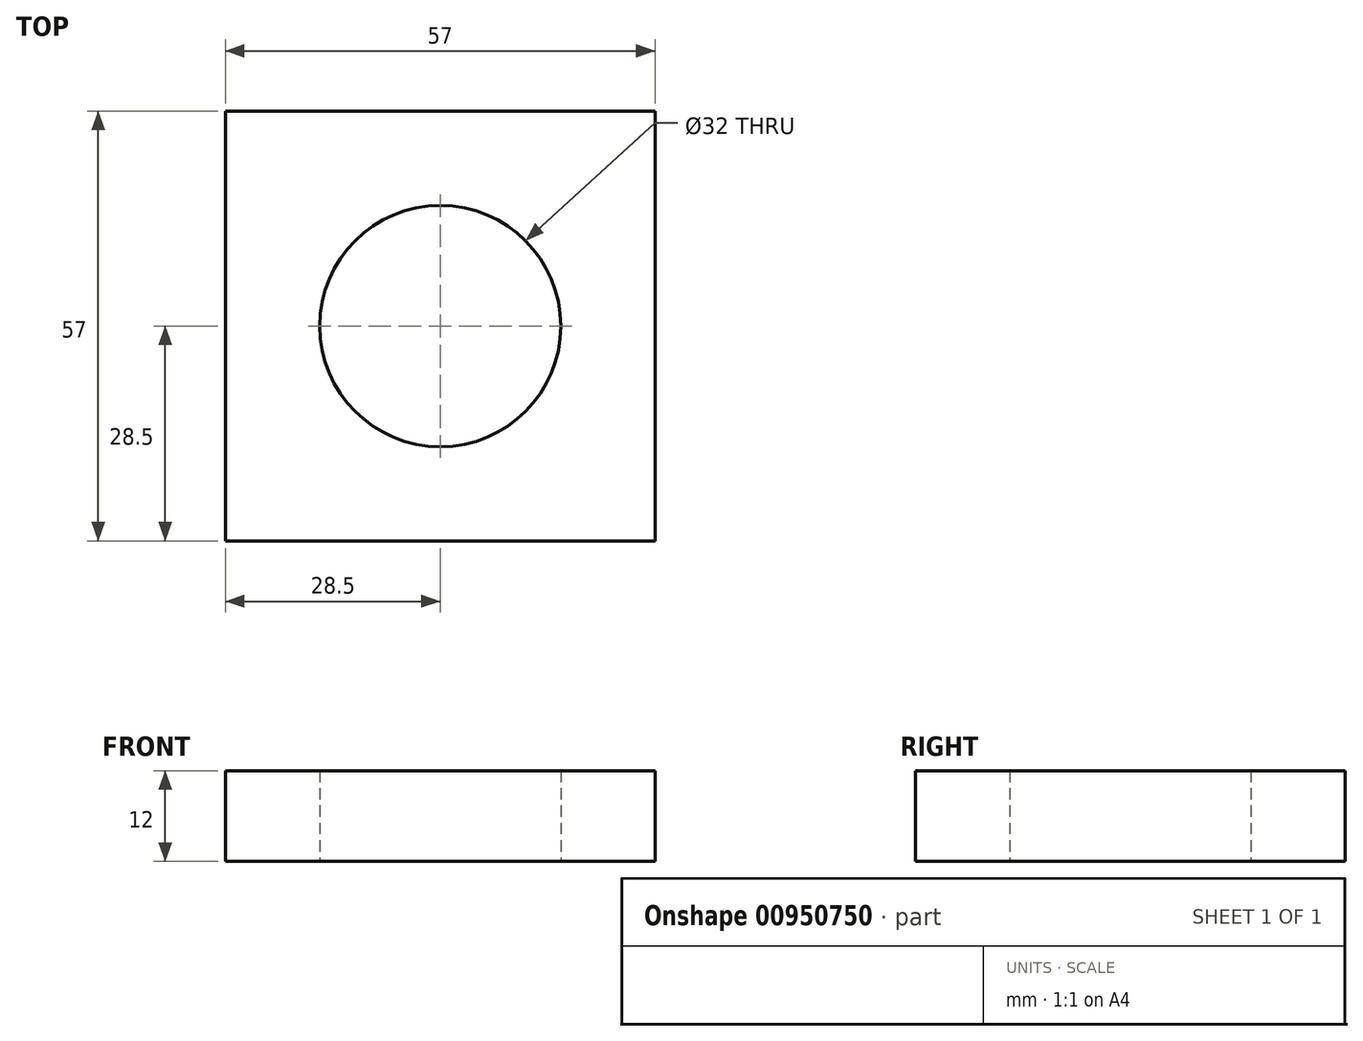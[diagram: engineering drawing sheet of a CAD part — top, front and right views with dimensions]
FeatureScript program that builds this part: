
annotation { "Feature Type Name" : "Feature", "Feature Type Description" : "" }
export const myFeature = defineFeature(function(context is Context, id is Id, definition is map)
    precondition{}
    {
        {
            var Q0;
            Q0=qCreatedBy(makeId("Top.planeOp"), FACE);
            var sketch = newSketch(context, id + "F0", { "sketchPlane" : qUnion([Q0])});
            skCircle(sketch, "E0", {"center": v(0, 0) * mm, "radius": 16 * mm});
            skFitSpline(sketch, "E1.0", {"points": [v(5.85, 0) * mm, v(5.85, 0.17) * mm, v(5.82, 0.5) * mm, v(5.75, 1) * mm, v(5.63, 1.48) * mm, v(5.47, 1.96) * mm, v(5.27, 2.42) * mm, v(5.04, 2.85) * mm, v(4.76, 3.27) * mm, v(4.46, 3.66) * mm, v(4.12, 4.02) * mm, v(3.75, 4.35) * mm, v(3.36, 4.65) * mm, v(2.94, 4.9) * mm, v(2.5, 5.13) * mm, v(2.05, 5.32) * mm, v(1.58, 5.46) * mm, v(1.1, 5.57) * mm, v(0.62, 5.63) * mm, v(0.14, 5.65) * mm, v(-0.35, 5.63) * mm, v(-0.83, 5.57) * mm, v(-1.3, 5.46) * mm, v(-1.76, 5.32) * mm, v(-2.2, 5.14) * mm, v(-2.63, 4.92) * mm, v(-3.04, 4.67) * mm, v(-3.42, 4.38) * mm, v(-3.78, 4.06) * mm, v(-4.1, 3.72) * mm, v(-4.4, 3.35) * mm, v(-4.66, 2.95) * mm, v(-4.88, 2.53) * mm, v(-5.07, 2.1) * mm, v(-5.22, 1.65) * mm, v(-5.34, 1.2) * mm, v(-5.4, 0.73) * mm, v(-5.44, 0.27) * mm, v(-5.43, -0.2) * mm, v(-5.38, -0.66) * mm, v(-5.3, -1.12) * mm, v(-5.17, -1.57) * mm, v(-5, -2) * mm, v(-4.8, -2.42) * mm, v(-4.57, -2.81) * mm, v(-4.3, -3.19) * mm, v(-4, -3.54) * mm, v(-3.68, -3.86) * mm, v(-3.32, -4.15) * mm, v(-2.95, -4.41) * mm, v(-2.55, -4.64) * mm, v(-2.14, -4.83) * mm, v(-1.72, -4.99) * mm, v(-1.28, -5.1) * mm, v(-0.83, -5.18) * mm, v(-0.39, -5.23) * mm, v(0.06, -5.23) * mm, v(0.51, -5.2) * mm, v(0.95, -5.12) * mm, v(1.39, -5) * mm, v(1.8, -4.86) * mm, v(2.21, -4.67) * mm, v(2.6, -4.46) * mm, v(2.96, -4.2) * mm, v(3.3, -3.93) * mm, v(3.62, -3.62) * mm, v(3.91, -3.3) * mm, v(4.17, -2.94) * mm, v(4.4, -2.56) * mm, v(4.6, -2.17) * mm, v(4.75, -1.77) * mm, v(4.87, -1.35) * mm, v(4.96, -0.92) * mm, v(5, -0.5) * mm, v(5.02, -0.06) * mm, v(5, 0.37) * mm, v(4.94, 0.8) * mm, v(4.84, 1.21) * mm, v(4.7, 1.62) * mm, v(4.54, 2.01) * mm, v(4.34, 2.39) * mm, v(4.1, 2.75) * mm, v(3.85, 3.08) * mm, v(3.56, 3.4) * mm, v(3.25, 3.68) * mm, v(2.92, 3.93) * mm, v(2.56, 4.16) * mm, v(2.2, 4.35) * mm, v(1.8, 4.51) * mm, v(1.4, 4.64) * mm, v(1, 4.73) * mm, v(0.6, 4.8) * mm, v(0.18, 4.81) * mm, v(-0.24, 4.8) * mm, v(-0.65, 4.75) * mm, v(-1.05, 4.67) * mm, v(-1.44, 4.55) * mm, v(-1.82, 4.4) * mm, v(-2.19, 4.21) * mm, v(-2.53, 4) * mm, v(-2.86, 3.76) * mm, v(-3.17, 3.5) * mm, v(-3.44, 3.2) * mm, v(-3.7, 2.89) * mm, v(-3.92, 2.55) * mm, v(-4.12, 2.2) * mm, v(-4.28, 1.83) * mm, v(-4.41, 1.46) * mm, v(-4.5, 1.07) * mm, v(-4.57, 0.68) * mm, v(-4.6, 0.28) * mm, v(-4.6, -0.11) * mm, v(-4.56, -0.5) * mm, v(-4.49, -0.9) * mm, v(-4.38, -1.27) * mm, v(-4.25, -1.64) * mm, v(-4.08, -2) * mm, v(-3.89, -2.33) * mm, v(-3.66, -2.65) * mm, v(-3.41, -2.94) * mm, v(-3.14, -3.22) * mm, v(-2.84, -3.47) * mm, v(-2.53, -3.69) * mm, v(-2.2, -3.88) * mm, v(-1.85, -4.05) * mm, v(-1.5, -4.18) * mm, v(-1.13, -4.28) * mm, v(-0.75, -4.35) * mm, v(-0.38, -4.39) * mm, v(-0.13, -4.4) * mm, v(0.25, -4.38) * mm, v(0.5, -4.35) * mm, v(1, -4.25) * mm, v(1.23, -4.18) * mm, v(1.7, -4) * mm, v(1.92, -3.89) * mm, v(2.34, -3.63) * mm, v(2.54, -3.48) * mm, v(2.91, -3.16) * mm, v(3.08, -2.98) * mm, v(3.39, -2.6) * mm, v(3.53, -2.4) * mm, v(3.76, -1.97) * mm, v(3.86, -1.75) * mm, v(4.02, -1.3) * mm, v(4.08, -1.06) * mm, v(4.16, -0.58) * mm, v(4.18, -0.34) * mm, v(4.18, 0.14) * mm, v(4.16, 0.38) * mm, v(4.07, 0.84) * mm, v(4, 1.07) * mm, v(3.85, 1.52) * mm, v(3.75, 1.73) * mm, v(3.5, 2.14) * mm, v(3.37, 2.34) * mm, v(3.07, 2.7) * mm, v(2.9, 2.86) * mm, v(2.55, 3.16) * mm, v(2.36, 3.3) * mm, v(1.96, 3.53) * mm, v(1.75, 3.63) * mm, v(1.32, 3.8) * mm, v(1.1, 3.86) * mm, v(0.65, 3.94) * mm, v(0.42, 3.97) * mm, v(-0.03, 3.97) * mm, v(-0.26, 3.96) * mm, v(-0.7, 3.89) * mm, v(-0.93, 3.83) * mm, v(-1.35, 3.69) * mm, v(-1.56, 3.6) * mm, v(-1.95, 3.38) * mm, v(-2.14, 3.26) * mm, v(-2.49, 2.98) * mm, v(-2.65, 2.83) * mm, v(-2.94, 2.5) * mm, v(-3.08, 2.32) * mm, v(-3.3, 1.95) * mm, v(-3.4, 1.75) * mm, v(-3.57, 1.34) * mm, v(-3.63, 1.13) * mm, v(-3.73, 0.7) * mm, v(-3.75, 0.5) * mm, v(-3.77, 0.06) * mm, v(-3.76, -0.15) * mm, v(-3.7, -0.58) * mm, v(-3.65, -0.79) * mm, v(-3.53, -1.2) * mm, v(-3.44, -1.4) * mm, v(-3.25, -1.77) * mm, v(-3.14, -1.95) * mm, v(-2.88, -2.29) * mm, v(-2.74, -2.44) * mm, v(-2.43, -2.73) * mm, v(-2.27, -2.86) * mm, v(-1.92, -3.08) * mm, v(-1.73, -3.18) * mm, v(-1.35, -3.35) * mm, v(-1.16, -3.41) * mm, v(-0.76, -3.5) * mm, v(-0.55, -3.54) * mm, v(-0.15, -3.56) * mm, v(0.06, -3.55) * mm, v(0.46, -3.5) * mm, v(0.66, -3.47) * mm, v(1.05, -3.36) * mm, v(1.24, -3.28) * mm, v(1.6, -3.1) * mm, v(1.77, -3) * mm, v(2.1, -2.77) * mm, v(2.24, -2.64) * mm, v(2.52, -2.36) * mm, v(2.64, -2.2) * mm, v(2.86, -1.88) * mm, v(2.96, -1.7) * mm, v(3.12, -1.35) * mm, v(3.19, -1.17) * mm, v(3.29, -0.8) * mm, v(3.32, -0.6) * mm, v(3.35, -0.22) * mm, v(3.35, -0.03) * mm, v(3.32, 0.35) * mm, v(3.28, 0.54) * mm, v(3.18, 0.9) * mm, v(3.12, 1.09) * mm, v(2.96, 1.43) * mm, v(2.87, 1.6) * mm, v(2.65, 1.9) * mm, v(2.53, 2.05) * mm, v(2.27, 2.31) * mm, v(2.13, 2.43) * mm, v(1.83, 2.65) * mm, v(1.67, 2.74) * mm, v(1.34, 2.9) * mm, v(1.17, 2.97) * mm, v(0.82, 3.07) * mm, v(0.64, 3.1) * mm, v(0.28, 3.14) * mm, v(0.1, 3.14) * mm, v(-0.26, 3.12) * mm, v(-0.43, 3.1) * mm, v(-0.78, 3) * mm, v(-0.95, 2.95) * mm, v(-1.27, 2.8) * mm, v(-1.43, 2.72) * mm, v(-1.72, 2.53) * mm, v(-1.86, 2.42) * mm, v(-2.11, 2.18) * mm, v(-2.23, 2.05) * mm, v(-2.44, 1.78) * mm, v(-2.53, 1.63) * mm, v(-2.68, 1.32) * mm, v(-2.75, 1.16) * mm, v(-2.85, 0.84) * mm, v(-2.88, 0.67) * mm, v(-2.93, 0.34) * mm, v(-2.93, 0.17) * mm, v(-2.92, -0.17) * mm, v(-2.9, -0.33) * mm, v(-2.82, -0.66) * mm, v(-2.77, -0.82) * mm, v(-2.65, -1.12) * mm, v(-2.57, -1.27) * mm, v(-2.4, -1.55) * mm, v(-2.3, -1.68) * mm, v(-2.08, -1.92) * mm, v(-1.96, -2.03) * mm, v(-1.7, -2.23) * mm, v(-1.57, -2.32) * mm, v(-1.3, -2.47) * mm, v(-1.15, -2.53) * mm, v(-0.84, -2.63) * mm, v(-0.7, -2.67) * mm, v(-0.38, -2.71) * mm, v(-0.22, -2.72) * mm, v(0.09, -2.71) * mm, v(0.24, -2.7) * mm, v(0.55, -2.64) * mm, v(0.7, -2.6) * mm, v(0.98, -2.48) * mm, v(1.12, -2.42) * mm, v(1.38, -2.26) * mm, v(1.5, -2.17) * mm, v(1.73, -1.97) * mm, v(1.84, -1.87) * mm, v(2.02, -1.63) * mm, v(2.1, -1.51) * mm, v(2.25, -1.25) * mm, v(2.32, -1.12) * mm, v(2.41, -0.84) * mm, v(2.45, -0.7) * mm, v(2.5, -0.41) * mm, v(2.51, -0.27) * mm, v(2.51, 0.02) * mm, v(2.5, 0.16) * mm, v(2.45, 0.45) * mm, v(2.41, 0.58) * mm, v(2.31, 0.85) * mm, v(2.25, 0.98) * mm, v(2.11, 1.22) * mm, v(2.03, 1.34) * mm, v(1.86, 1.55) * mm, v(1.76, 1.65) * mm, v(1.55, 1.83) * mm, v(1.44, 1.9) * mm, v(1.2, 2.05) * mm, v(1.08, 2.1) * mm, v(0.83, 2.2) * mm, v(0.7, 2.24) * mm, v(0.44, 2.29) * mm, v(0.3, 2.3) * mm, v(0.04, 2.3) * mm, v(-0.1, 2.3) * mm, v(-0.35, 2.25) * mm, v(-0.48, 2.22) * mm, v(-0.73, 2.14) * mm, v(-0.84, 2.09) * mm, v(-1.07, 1.96) * mm, v(-1.18, 1.9) * mm, v(-1.38, 1.73) * mm, v(-1.47, 1.65) * mm, v(-1.63, 1.46) * mm, v(-1.7, 1.36) * mm, v(-1.84, 1.14) * mm, v(-1.9, 1.03) * mm, v(-1.99, 0.8) * mm, v(-2.02, 0.69) * mm, v(-2.07, 0.45) * mm, v(-2.09, 0.33) * mm, v(-2.1, 0.09) * mm, v(-2.1, -0.03) * mm, v(-2.06, -0.27) * mm, v(-2.03, -0.39) * mm, v(-1.96, -0.61) * mm, v(-1.91, -0.72) * mm, v(-1.8, -0.93) * mm, v(-1.74, -1.03) * mm, v(-1.6, -1.2) * mm, v(-1.52, -1.3) * mm, v(-1.36, -1.45) * mm, v(-1.27, -1.52) * mm, v(-1.08, -1.64) * mm, v(-0.98, -1.7) * mm, v(-0.77, -1.78) * mm, v(-0.66, -1.81) * mm, v(-0.45, -1.86) * mm, v(-0.34, -1.88) * mm, v(-0.12, -1.89) * mm, v(-0.01, -1.88) * mm, v(0.2, -1.86) * mm, v(0.3, -1.84) * mm, v(0.5, -1.78) * mm, v(0.6, -1.74) * mm, v(0.8, -1.64) * mm, v(0.88, -1.59) * mm, v(1.05, -1.46) * mm, v(1.13, -1.4) * mm, v(1.27, -1.25) * mm, v(1.33, -1.17) * mm, v(1.44, -1) * mm, v(1.5, -0.9) * mm, v(1.57, -0.73) * mm, v(1.6, -0.63) * mm, v(1.65, -0.44) * mm, v(1.67, -0.35) * mm, v(1.68, -0.15) * mm, v(1.68, -0.05) * mm, v(1.66, 0.14) * mm, v(1.64, 0.23) * mm, v(1.59, 0.41) * mm, v(1.55, 0.5) * mm, v(1.47, 0.67) * mm, v(1.43, 0.75) * mm, v(1.32, 0.9) * mm, v(1.26, 0.97) * mm, v(1.13, 1.1) * mm, v(1.06, 1.15) * mm, v(0.91, 1.25) * mm, v(0.83, 1.3) * mm, v(0.67, 1.37) * mm, v(0.6, 1.4) * mm, v(0.42, 1.44) * mm, v(0.34, 1.46) * mm, v(0.17, 1.47) * mm, v(0.08, 1.47) * mm, v(-0.08, 1.45) * mm, v(-0.17, 1.44) * mm, v(-0.33, 1.4) * mm, v(-0.4, 1.37) * mm, v(-0.55, 1.3) * mm, v(-0.62, 1.26) * mm, v(-0.75, 1.17) * mm, v(-0.81, 1.12) * mm, v(-0.93, 1) * mm, v(-0.98, 0.94) * mm, v(-1.07, 0.82) * mm, v(-1.1, 0.75) * mm, v(-1.17, 0.61) * mm, v(-1.2, 0.54) * mm, v(-1.23, 0.4) * mm, v(-1.25, 0.32) * mm, v(-1.26, 0.18) * mm, v(-1.26, 0.1) * mm, v(-1.25, -0.04) * mm, v(-1.24, -0.11) * mm, v(-1.2, -0.25) * mm, v(-1.18, -0.32) * mm, v(-1.12, -0.44) * mm, v(-1.09, -0.5) * mm, v(-1, -0.62) * mm, v(-0.97, -0.67) * mm, v(-0.87, -0.76) * mm, v(-0.82, -0.8) * mm, v(-0.71, -0.88) * mm, v(-0.66, -0.92) * mm, v(-0.54, -0.97) * mm, v(-0.48, -1) * mm, v(-0.36, -1.03) * mm, v(-0.3, -1.04) * mm, v(-0.17, -1.05) * mm, v(-0.11, -1.05) * mm, v(0, -1.05) * mm, v(0.07, -1.04) * mm, v(0.18, -1) * mm, v(0.24, -0.99) * mm, v(0.34, -0.94) * mm, v(0.4, -0.9) * mm, v(0.49, -0.85) * mm, v(0.53, -0.8) * mm, v(0.61, -0.73) * mm, v(0.65, -0.7) * mm, v(0.71, -0.6) * mm, v(0.74, -0.56) * mm, v(0.78, -0.46) * mm, v(0.8, -0.41) * mm, v(0.83, -0.31) * mm, v(0.84, -0.26) * mm, v(0.85, -0.16) * mm, v(0.85, -0.11) * mm, v(0.84, -0.01) * mm, v(0.83, 0.03) * mm, v(0.8, 0.13) * mm, v(0.8, 0.17) * mm, v(0.75, 0.26) * mm, v(0.73, 0.3) * mm, v(0.68, 0.37) * mm, v(0.65, 0.4) * mm, v(0.59, 0.47) * mm, v(0.55, 0.5) * mm, v(0.48, 0.54) * mm, v(0.45, 0.56) * mm, v(0.37, 0.6) * mm, v(0.33, 0.6) * mm, v(0.25, 0.63) * mm, v(0.22, 0.64) * mm, v(0.14, 0.64) * mm, v(0.1, 0.64) * mm, v(0.03, 0.63) * mm, v(-0.01, 0.63) * mm, v(-0.08, 0.6) * mm, v(-0.11, 0.6) * mm, v(-0.18, 0.56) * mm, v(-0.2, 0.54) * mm, v(-0.26, 0.5) * mm, v(-0.28, 0.48) * mm, v(-0.33, 0.43) * mm, v(-0.35, 0.4) * mm, v(-0.38, 0.35) * mm, v(-0.4, 0.33) * mm, v(-0.41, 0.27) * mm, v(-0.42, 0.24) * mm, v(-0.43, 0.19) * mm, v(-0.44, 0.16) * mm, v(-0.44, 0.1) * mm, v(-0.44, 0.08) * mm, v(-0.43, 0.03) * mm, v(-0.42, 0) * mm, v(-0.4, -0.04) * mm, v(-0.4, -0.07) * mm, v(-0.37, -0.1) * mm, v(-0.35, -0.12) * mm, v(-0.32, -0.16) * mm, v(-0.3, -0.17) * mm, v(-0.27, -0.2) * mm, v(-0.25, -0.2) * mm, v(-0.22, -0.22) * mm, v(-0.2, -0.23) * mm, v(-0.16, -0.24) * mm, v(-0.15, -0.24) * mm, v(-0.11, -0.24) * mm, v(-0.1, -0.24) * mm, v(-0.06, -0.24) * mm, v(-0.05, -0.23) * mm, v(-0.02, -0.22) * mm, v(0, -0.21) * mm, v(0.02, -0.2) * mm, v(0.03, -0.19) * mm, v(0.04, -0.17) * mm, v(0.05, -0.16) * mm, v(0.06, -0.14) * mm, v(0.07, -0.13) * mm, v(0.07, -0.1) * mm, v(0.07, -0.1) * mm, v(0.07, -0.08) * mm, v(0.07, -0.06) * mm, v(0.06, -0.04) * mm, v(0.05, -0.03) * mm, v(0.05, -0.02) * mm, v(0.04, -0.01) * mm, v(0.03, 0) * mm, v(0.02, 0) * mm, v(0, 0) * mm, v(0, 0) * mm]});
            skCircle(sketch, "E2.0", {"center": v(0, 0) * mm, "radius": 5.85 * mm});
            skLineSegment(sketch, "E3", {"start": v(5.28, -2.53) * mm, "end": v(0, 0) * mm});
            skSolve(sketch);
        }
        {
            var Q0;
            Q0=qCreatedBy(makeId("Top.planeOp"), FACE);
            var sketch = newSketch(context, id + "F1", { "sketchPlane" : qUnion([Q0])});
            skLineSegment(sketch, "E4.bottom", {"start": v(28.5, 28.5) * mm, "end": v(-28.5, 28.5) * mm});
            skLineSegment(sketch, "E4.top", {"start": v(28.5, -28.5) * mm, "end": v(-28.5, -28.5) * mm});
            skLineSegment(sketch, "E4.left", {"start": v(28.5, 28.5) * mm, "end": v(28.5, -28.5) * mm});
            skLineSegment(sketch, "E4.right", {"start": v(-28.5, 28.5) * mm, "end": v(-28.5, -28.5) * mm});
            skPoint(sketch, "E4.middle", {"position": v(0, 0) * mm});
            skCircle(sketch, "E5.0", {"center": v(0, 0) * mm, "radius": 16 * mm});
            skCircle(sketch, "E6.0", {"center": v(0, 0) * mm, "radius": 5.85 * mm});
            skFitSpline(sketch, "E7.0", {"points": [v(5.85, 0) * mm, v(5.83, 0.29) * mm, v(5.8, 0.57) * mm, v(5.68, 1.13) * mm, v(5.6, 1.4) * mm, v(5.41, 1.94) * mm, v(5.3, 2.2) * mm, v(5.03, 2.69) * mm, v(4.88, 2.93) * mm, v(4.54, 3.37) * mm, v(4.36, 3.58) * mm, v(3.97, 3.97) * mm, v(3.76, 4.15) * mm, v(3.32, 4.47) * mm, v(3.08, 4.62) * mm, v(2.6, 4.87) * mm, v(2.35, 4.98) * mm, v(1.84, 5.16) * mm, v(1.58, 5.23) * mm, v(1.06, 5.33) * mm, v(0.8, 5.36) * mm, v(0.26, 5.38) * mm, v(0, 5.37) * mm, v(-0.52, 5.31) * mm, v(-0.78, 5.27) * mm, v(-1.29, 5.13) * mm, v(-1.53, 5.05) * mm, v(-2, 4.85) * mm, v(-2.24, 4.73) * mm, v(-2.67, 4.46) * mm, v(-2.88, 4.31) * mm, v(-3.27, 3.98) * mm, v(-3.45, 3.8) * mm, v(-3.79, 3.43) * mm, v(-3.94, 3.23) * mm, v(-4.21, 2.81) * mm, v(-4.33, 2.6) * mm, v(-4.54, 2.15) * mm, v(-4.62, 1.91) * mm, v(-4.76, 1.44) * mm, v(-4.8, 1.2) * mm, v(-4.87, 0.72) * mm, v(-4.89, 0.48) * mm, v(-4.88, 0) * mm, v(-4.86, -0.24) * mm, v(-4.78, -0.71) * mm, v(-4.73, -0.94) * mm, v(-4.58, -1.4) * mm, v(-4.5, -1.6) * mm, v(-4.29, -2.03) * mm, v(-4.17, -2.23) * mm, v(-3.9, -2.61) * mm, v(-3.76, -2.8) * mm, v(-3.45, -3.12) * mm, v(-3.28, -3.28) * mm, v(-2.92, -3.56) * mm, v(-2.73, -3.69) * mm, v(-2.34, -3.91) * mm, v(-2.14, -4) * mm, v(-1.73, -4.17) * mm, v(-1.51, -4.24) * mm, v(-1.09, -4.34) * mm, v(-0.87, -4.37) * mm, v(-0.43, -4.4) * mm, v(-0.22, -4.4) * mm, v(0.22, -4.37) * mm, v(0.43, -4.34) * mm, v(0.85, -4.25) * mm, v(1.05, -4.19) * mm, v(1.44, -4.04) * mm, v(1.64, -3.95) * mm, v(2, -3.74) * mm, v(2.17, -3.62) * mm, v(2.5, -3.37) * mm, v(2.65, -3.23) * mm, v(2.93, -2.93) * mm, v(3.06, -2.78) * mm, v(3.3, -2.44) * mm, v(3.4, -2.27) * mm, v(3.58, -1.91) * mm, v(3.65, -1.73) * mm, v(3.78, -1.35) * mm, v(3.82, -1.16) * mm, v(3.89, -0.77) * mm, v(3.9, -0.58) * mm, v(3.92, -0.2) * mm, v(3.9, 0) * mm, v(3.86, 0.38) * mm, v(3.82, 0.57) * mm, v(3.71, 0.93) * mm, v(3.65, 1.1) * mm, v(3.5, 1.45) * mm, v(3.4, 1.61) * mm, v(3.2, 1.92) * mm, v(3.1, 2.07) * mm, v(2.85, 2.34) * mm, v(2.72, 2.47) * mm, v(2.45, 2.7) * mm, v(2.3, 2.8) * mm, v(2, 3) * mm, v(1.84, 3.07) * mm, v(1.52, 3.21) * mm, v(1.35, 3.27) * mm, v(1.02, 3.36) * mm, v(0.85, 3.39) * mm, v(0.5, 3.43) * mm, v(0.34, 3.43) * mm, v(0, 3.42) * mm, v(-0.17, 3.4) * mm, v(-0.5, 3.33) * mm, v(-0.66, 3.3) * mm, v(-0.97, 3.18) * mm, v(-1.12, 3.12) * mm, v(-1.4, 2.96) * mm, v(-1.54, 2.88) * mm, v(-1.8, 2.69) * mm, v(-1.92, 2.58) * mm, v(-2.14, 2.36) * mm, v(-2.24, 2.24) * mm, v(-2.43, 2) * mm, v(-2.51, 1.86) * mm, v(-2.66, 1.6) * mm, v(-2.72, 1.45) * mm, v(-2.82, 1.17) * mm, v(-2.86, 1.02) * mm, v(-2.91, 0.73) * mm, v(-2.93, 0.58) * mm, v(-2.94, 0.29) * mm, v(-2.94, 0.14) * mm, v(-2.9, -0.14) * mm, v(-2.88, -0.28) * mm, v(-2.81, -0.56) * mm, v(-2.77, -0.7) * mm, v(-2.66, -0.95) * mm, v(-2.6, -1.07) * mm, v(-2.45, -1.3) * mm, v(-2.37, -1.42) * mm, v(-2.2, -1.63) * mm, v(-2.1, -1.72) * mm, v(-1.9, -1.9) * mm, v(-1.8, -1.98) * mm, v(-1.57, -2.12) * mm, v(-1.46, -2.18) * mm, v(-1.22, -2.29) * mm, v(-1.1, -2.33) * mm, v(-0.86, -2.4) * mm, v(-0.73, -2.42) * mm, v(-0.49, -2.45) * mm, v(-0.36, -2.46) * mm, v(-0.12, -2.45) * mm, v(0, -2.44) * mm, v(0.24, -2.4) * mm, v(0.35, -2.37) * mm, v(0.58, -2.3) * mm, v(0.68, -2.25) * mm, v(0.89, -2.14) * mm, v(0.99, -2.08) * mm, v(1.17, -1.95) * mm, v(1.25, -1.88) * mm, v(1.41, -1.72) * mm, v(1.49, -1.64) * mm, v(1.62, -1.46) * mm, v(1.67, -1.37) * mm, v(1.78, -1.19) * mm, v(1.82, -1.09) * mm, v(1.89, -0.9) * mm, v(1.92, -0.8) * mm, v(1.96, -0.6) * mm, v(1.97, -0.5) * mm, v(1.98, -0.3) * mm, v(1.97, -0.2) * mm, v(1.95, 0) * mm, v(1.93, 0.1) * mm, v(1.89, 0.28) * mm, v(1.85, 0.37) * mm, v(1.78, 0.54) * mm, v(1.74, 0.62) * mm, v(1.64, 0.78) * mm, v(1.59, 0.85) * mm, v(1.47, 0.98) * mm, v(1.4, 1.05) * mm, v(1.28, 1.16) * mm, v(1.2, 1.2) * mm, v(1.06, 1.3) * mm, v(0.99, 1.34) * mm, v(0.84, 1.4) * mm, v(0.76, 1.43) * mm, v(0.6, 1.47) * mm, v(0.53, 1.48) * mm, v(0.37, 1.5) * mm, v(0.3, 1.5) * mm, v(0.15, 1.49) * mm, v(0.07, 1.48) * mm, v(-0.07, 1.45) * mm, v(-0.14, 1.43) * mm, v(-0.27, 1.38) * mm, v(-0.34, 1.35) * mm, v(-0.46, 1.28) * mm, v(-0.51, 1.24) * mm, v(-0.62, 1.16) * mm, v(-0.67, 1.11) * mm, v(-0.75, 1.02) * mm, v(-0.8, 0.97) * mm, v(-0.86, 0.86) * mm, v(-0.9, 0.8) * mm, v(-0.94, 0.7) * mm, v(-0.96, 0.64) * mm, v(-1, 0.53) * mm, v(-1, 0.48) * mm, v(-1.02, 0.36) * mm, v(-1.02, 0.3) * mm, v(-1.02, 0.2) * mm, v(-1.01, 0.15) * mm, v(-1, 0.05) * mm, v(-0.98, 0) * mm, v(-0.94, -0.1) * mm, v(-0.92, -0.14) * mm, v(-0.87, -0.22) * mm, v(-0.85, -0.26) * mm, v(-0.79, -0.33) * mm, v(-0.76, -0.36) * mm, v(-0.7, -0.42) * mm, v(-0.66, -0.44) * mm, v(-0.59, -0.48) * mm, v(-0.55, -0.5) * mm, v(-0.48, -0.53) * mm, v(-0.44, -0.54) * mm, v(-0.37, -0.56) * mm, v(-0.34, -0.56) * mm, v(-0.27, -0.57) * mm, v(-0.23, -0.56) * mm, v(-0.17, -0.55) * mm, v(-0.14, -0.55) * mm, v(-0.08, -0.53) * mm, v(-0.05, -0.52) * mm, v(0, -0.49) * mm, v(0.02, -0.47) * mm, v(0.07, -0.44) * mm, v(0.08, -0.42) * mm, v(0.12, -0.38) * mm, v(0.13, -0.36) * mm, v(0.15, -0.32) * mm, v(0.16, -0.3) * mm, v(0.17, -0.25) * mm, v(0.17, -0.23) * mm, v(0.17, -0.2) * mm, v(0.17, -0.17) * mm, v(0.17, -0.13) * mm, v(0.16, -0.12) * mm, v(0.14, -0.09) * mm, v(0.13, -0.07) * mm, v(0.11, -0.05) * mm, v(0.1, -0.04) * mm, v(0.07, -0.02) * mm, v(0.06, -0.01) * mm, v(0.03, 0) * mm, v(0.02, 0) * mm, v(0, 0) * mm]});
            skLineSegment(sketch, "E8.0", {"start": v(5.4, -2.23) * mm, "end": v(0, 0) * mm});
            skSolve(sketch);
        }
        {
            var Q0;
            Q0 = qSketchRegion(id + "F1", true);
            extrude(context, id + "F2", {"entities" : qUnion([Q0]), "depth" : 12 * mm, "offsetDistance" : 25 * mm});
        }
    });
